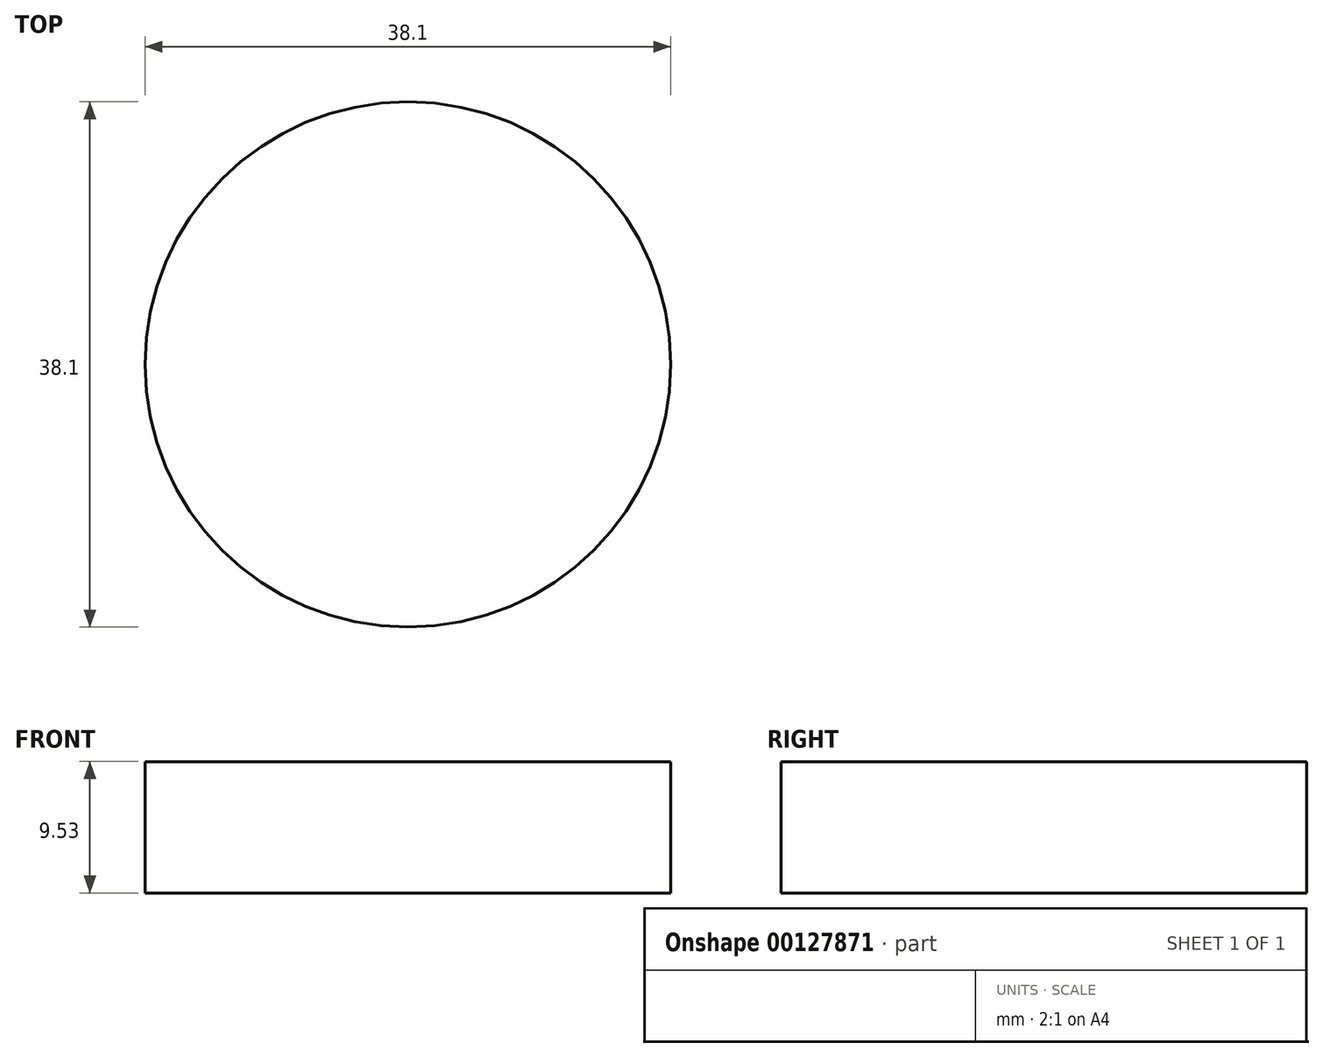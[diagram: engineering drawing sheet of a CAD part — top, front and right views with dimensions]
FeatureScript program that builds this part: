
annotation { "Feature Type Name" : "Feature", "Feature Type Description" : "" }
export const myFeature = defineFeature(function(context is Context, id is Id, definition is map)
    precondition{}
    {
        {
            var Q0;
            Q0=qCreatedBy(makeId("Top.planeOp"),FACE);
            var sketch = newSketch(context, id + "F0", { "sketchPlane" : qUnion([Q0])});
            skCircle(sketch, "E0", {"center": v(0, 0) * mm, "radius": 19.05 * mm});
            skSolve(sketch);
        }
        {
            var Q0;
            Q0=makeQuery(id+"F0.imprint","IMPRINT",FACE,{"disambiguationData":[TD([[makeQuery(id+"F0.imprint","IMPRINT",EDGE,{"derivedFrom":sQuery(id+"F0.wireOp",EDGE,"E0")}),1.0]])]});
            extrude(context, id + "F1", {"entities" : qUnion([Q0]), "depth" : 9.52 * mm});
        }
    });
